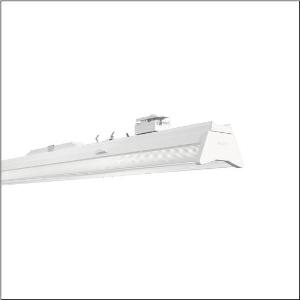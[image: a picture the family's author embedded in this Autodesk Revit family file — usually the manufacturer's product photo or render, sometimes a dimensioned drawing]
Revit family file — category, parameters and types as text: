
# Revit family: licross_r__11_performance_mo_51tm16dn35xg_3127
name_source: partatom
category: Lighting Fixtures
units: mm (PartAtom-declared; Revit-internal decimal feet)

## family parameters
Cut with Voids When Loaded = No
Host = Face
Light Source = No
Part Type = Normal
Room Calculation Point = No
Round Connector Dimension = Use Diameter
Shared = No

## types (1)
- --- (1 x LED, 5100 lm, 28.3 W, 3000K)
    Apparent Load = 28 VA
    CIE Flux Codes = 66 88 96 79 100
    Color Rendering = 80
    Color Temperature = 3000K
    Default Elevation = 1800 mm
    Description = Licross® 11 Performance MO, luminaire insert, of sheet steel, galvanised, coil coated, white, length: 1.500mm, width: 120mm, height: 123mm, LED rated luminous flux: 5.100lm, light colour: 830, control gear: DALI 2, with plug, 5-pole, with phase selection, mains connection: 220..240V, AC, 50/60Hz, rated input power: 28.3W, halogen-free wiring, primary light control with lens, of plastic, primary optical cover: cover, of PMMA, light emission: direct/indirect distribution, primary light characteristic: symmetric, protection rating (complete): IP40, insulation class (complete): insulation class I (protective earthing), certification: CE, ENEC, VDE, UKCA, protection symbol: D if used in an environment without relevant dust loads with corresponding accessories, impact resistance: IK06, permissible ambient temperature for indoor applications: -25..+45°C, corresponds to IFS (International Featured Standards) requirements for safety and quality in the food industry, reducing of maximum allowable ambient temperature of 5°C with ceiling mounting, LABS conformity tested according to VDMA 24364:2018-05, packaging unit: 1 piece
    Height = 114 mm
    Lamp = 1 x LED
    Lamp Light Flux = 5100 lm
    Lamp Power = 28.3 W
    Lamp count = 1
    Length = 1500 mm
    Luminous efficacy = 180 lm/W
    Manufacturer = Siteco
    ModVariant = No
    Model = 51TM16DN35XG
    Mounting Place = Ceiling
    Mounting Type = Pendant
    Number of Poles = 1
    OnlyDefault = Yes
    Power Factor = 1
    Product Name = Licross® 11 Performance MO
    Product group = luminaire insert
    ProductGroupID = 901
    Protection Class = Protection class I
    Protection Degree = IP 40
    RLX_Detail_Level = 1
    RLX_Emergency_Light_Flux = 0 lm
    RLX_Emergency_Type = 0
    RLX_Emergency_Type_DB = No
    RlxData = <blob elided: 33865 chars, md5=ebf25789>
    Socket = socket
    Standby Power = 0 W
    System Light Flux = 5100 lm
    System Power = 28 W
    Type Comments = factory setting: luminous flux: 100 % | dim-lin: 254 | 190 mA
    Type Image = l_1256138.jpg
    URL = http://relux.com
    VarID = @adj_026827
    Voltage = 0 V
    Weight = 0.00 kg
    Width = 120 mm

## geometry (parser evidence)
native form markers: Blend x4, Sweep x14
no freeform markers — native parametric forms only
